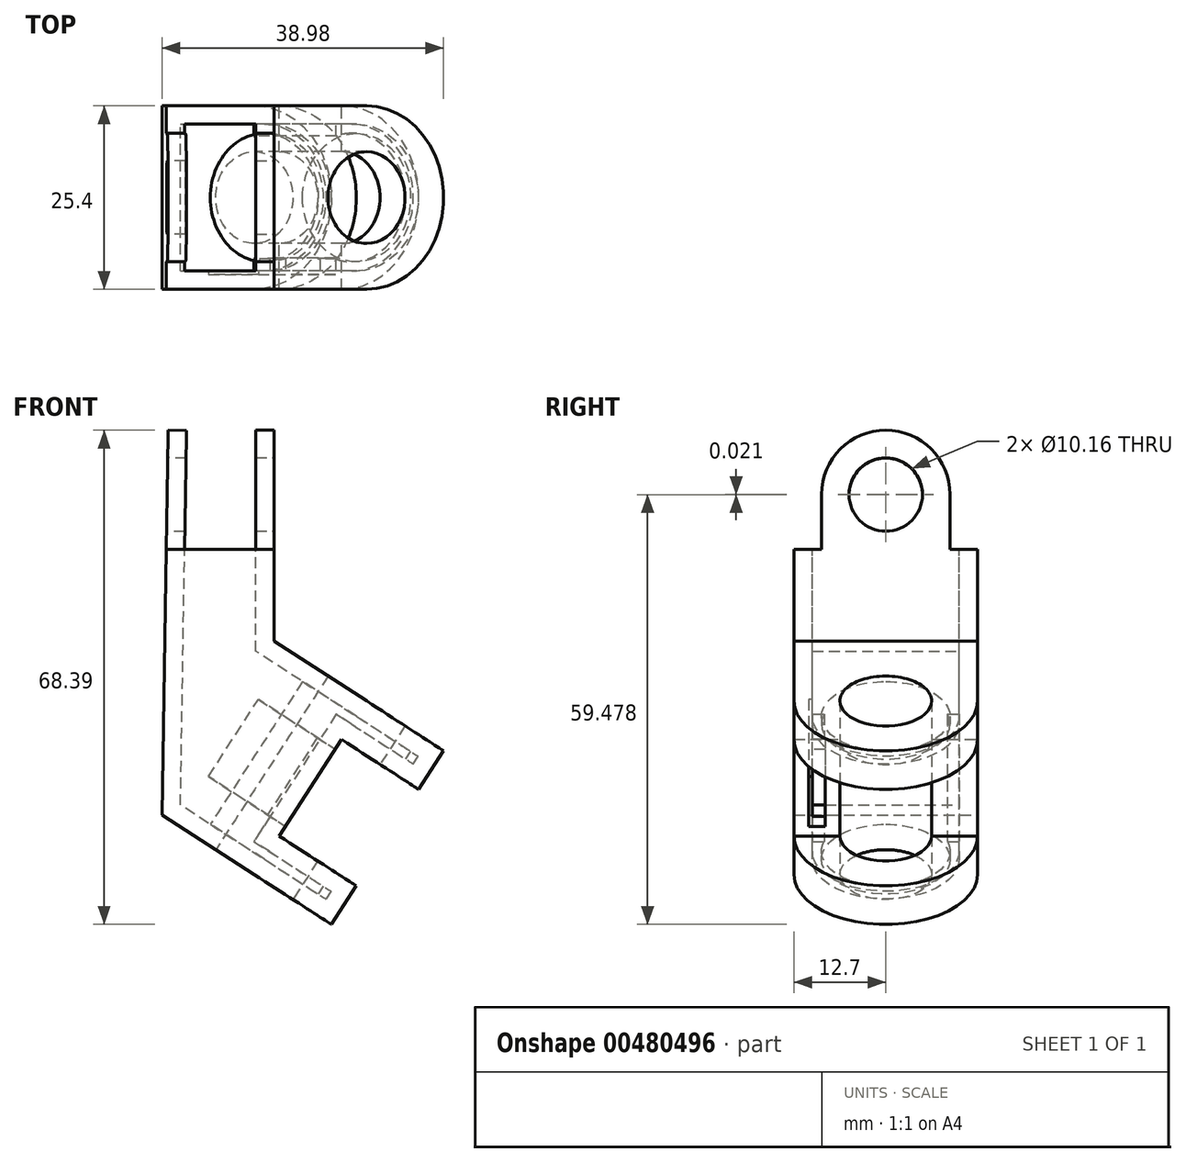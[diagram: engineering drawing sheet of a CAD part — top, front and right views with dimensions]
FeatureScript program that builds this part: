
annotation { "Feature Type Name" : "Feature", "Feature Type Description" : "" }
export const myFeature = defineFeature(function(context is Context, id is Id, definition is map)
    precondition{}
    {
        {
            var Q0;
            Q0=qCreatedBy(makeId("Front.planeOp"),FACE);
            var sketch = newSketch(context, id + "F0", { "sketchPlane" : qUnion([Q0])});
            skLineSegment(sketch, "E0", {"start": v(3.05, 0.95) * mm, "end": v(-9.73, 9.2) * mm});
            skLineSegment(sketch, "E1", {"start": v(-12.48, -23.08) * mm, "end": v(-25.26, -14.82) * mm});
            skLineSegment(sketch, "E2", {"start": v(-9.73, 9.2) * mm, "end": v(-9.73, 21.9) * mm});
            skLineSegment(sketch, "E3", {"start": v(-24.67, 21.9) * mm, "end": v(-9.73, 21.9) * mm});
            skLineSegment(sketch, "E4", {"start": v(-10.92, -20.66) * mm, "end": v(1.49, -1.46) * mm});
            skPoint(sketch, "E5.start.orphan", {"position": v(4.25, -16.85) * mm});
            skLineSegment(sketch, "E6", {"start": v(-10.92, -20.66) * mm, "end": v(-12.48, -23.08) * mm});
            skLineSegment(sketch, "E7", {"start": v(-12.48, -23.08) * mm, "end": v(3.05, 0.95) * mm});
            skPoint(sketch, "E8.orphan", {"position": v(-3.52, -28.87) * mm});
            skPoint(sketch, "E9.start.orphan", {"position": v(-1.96, -26.45) * mm});
            skPoint(sketch, "E10.start.orphan", {"position": v(10.45, -7.25) * mm});
            skPoint(sketch, "E11.orphan", {"position": v(12, -4.84) * mm});
            skLineSegment(sketch, "E12", {"start": v(-25.26, -14.82) * mm, "end": v(-24.67, 21.9) * mm});
            skSolve(sketch);
        }
        {
            var Q0;
            Q0 = qSketchRegion(id + "F0", true);
            extrude(context, id + "F1", {"entities" : qUnion([Q0]), "depth" : 25.4 * mm});
        }
        {
            var Q0;
            Q0=makeQuery(id+"F1.opExtrude","SWEPT_FACE",FACE,{"disambiguationData":[OSD([sQuery(id+"F0.wireOp",EDGE,"E0")])]});
            var sketch = newSketch(context, id + "F2", { "sketchPlane" : qUnion([Q0])});
            skLineSegment(sketch, "E13", {"start": v(2.04, -25.4) * mm, "end": v(2.04, -17.78) * mm});
            skArc(sketch, "E14", {"start": v(2.04, -25.4) * mm, "mid": v(14.74, -12.7) * mm, "end": v(2.04, 0) * mm});
            skCircle(sketch, "E15", {"center": v(2.04, -12.7) * mm, "radius": 5.08 * mm});
            skLineSegment(sketch, "E16.trimOffspring", {"start": v(2.04, -7.62) * mm, "end": v(2.04, 0) * mm});
            skSolve(sketch);
        }
        {
            var Q0;
            {var subQ0=sQuery(id+"F2.wireOp",EDGE,"E13");Q0=makeQuery(id+"F2.imprint","IMPRINT",FACE,{"disambiguationData":[TD([[makeQuery(id+"F2.imprint","IMPRINT",EDGE,{"derivedFrom":subQ0}),-1.0]])]});}
            extrude(context, id + "F3", {"entities" : qUnion([Q0]), "operationType" : NewBodyOperationType.ADD, "depth" : -6.35 * mm});
        }
        {
            var Q0;
            Q0=makeQuery(id+"F1.opExtrude","SWEPT_FACE",FACE,{"disambiguationData":[OSD([sQuery(id+"F0.wireOp",EDGE,"E1")])]});
            var sketch = newSketch(context, id + "F4", { "sketchPlane" : qUnion([Q0])});
            skArc(sketch, "E17", {"start": v(2.04, 0) * mm, "mid": v(14.74, 12.7) * mm, "end": v(2.04, 25.4) * mm});
            skCircle(sketch, "E18", {"center": v(2.04, 12.7) * mm, "radius": 6.35 * mm});
            skSolve(sketch);
        }
        {
            var Q0;
            {var subQ0=sQuery(id+"F4.wireOp",EDGE,"E17");Q0=makeQuery(id+"F4.imprint","IMPRINT",FACE,{"disambiguationData":[TD([[makeQuery(id+"F4.imprint","IMPRINT",EDGE,{"derivedFrom":subQ0}),1.0]])]});}
            extrude(context, id + "F5", {"entities" : qUnion([Q0]), "operationType" : NewBodyOperationType.ADD, "depth" : -6.35 * mm});
        }
        {
            var Q0;
            Q0=sQuery(id+"F4.wireOp",VERTEX,"E17.center");
            var Q1;
            Q1=makeQuery(id+"F1.opExtrude","SWEPT_BODY",BODY,{"disambiguationData":[OSD([sQuery(id+"F0.wireOp",EDGE,"E0"),sQuery(id+"F0.wireOp",EDGE,"E1"),sQuery(id+"F0.wireOp",EDGE,"E2"),sQuery(id+"F0.wireOp",EDGE,"91f72571-9d86-468c-b467-24505ed81b32"),sQuery(id+"F0.wireOp",EDGE,"E3"),sQuery(id+"F0.wireOp",EDGE,"E7")])]});
            hole(context, id + "F6", {"style" : HoleStyle.SIMPLE, "endStyle" : HoleEndStyle.THROUGH, "holeDiameter" : 12.7 * mm, "isTappedThrough" : true, "tappedDepth" : 12.7 * mm, "tapClearance" : 3, "locations" : qUnion([Q0]), "scope" : qUnion([Q1])});
        }
        {
            var Q0;
            Q0=makeQuery(id+"F1.opExtrude","SWEPT_FACE",FACE,{"disambiguationData":[OSD([sQuery(id+"F0.wireOp",EDGE,"E3")])]});
            shell(context, id + "F7", {"entities" : qUnion([Q0]), "thickness" : 2.54 * mm});
        }
        {
            var Q0;
            Q0=makeQuery(id+"F1.opExtrude","SWEPT_FACE",FACE,{"disambiguationData":[OSD([sQuery(id+"F0.wireOp",EDGE,"E2")])]});
            var sketch = newSketch(context, id + "F8", { "sketchPlane" : qUnion([Q0])});
            skLineSegment(sketch, "E19", {"start": v(-12.7, 21.9) * mm, "end": v(-12.7, 29.53) * mm});
            skLineSegment(sketch, "E20", {"start": v(-21.6, 21.9) * mm, "end": v(-21.6, 29.53) * mm});
            skLineSegment(sketch, "E21", {"start": v(-3.81, 21.9) * mm, "end": v(-3.81, 29.53) * mm});
            skArc(sketch, "E22", {"start": v(-3.8, 29.53) * mm, "mid": v(-12.7, 38.42) * mm, "end": v(-21.6, 29.53) * mm});
            skCircle(sketch, "E23", {"center": v(-12.7, 29.53) * mm, "radius": 5.08 * mm});
            skSolve(sketch);
        }
        {
            var Q0;
            {var subQ1=sQuery(id+"F8.wireOp",EDGE,"E20");Q0=makeQuery(id+"F8.imprint","IMPRINT",FACE,{"disambiguationData":[TD([[makeQuery(id+"F8.imprint","IMPRINT",EDGE,{"derivedFrom":subQ1}),-1.0]])]});}
            extrude(context, id + "F9", {"entities" : qUnion([Q0]), "operationType" : NewBodyOperationType.ADD, "depth" : -2.54 * mm});
        }
        {
            var Q0;
            Q0=makeQuery(id+"F1.opExtrude","SWEPT_FACE",FACE,{"disambiguationData":[OSD([sQuery(id+"F0.wireOp",EDGE,"E12")])]});
            var sketch = newSketch(context, id + "F10", { "sketchPlane" : qUnion([Q0])});
            skLineSegment(sketch, "E24", {"start": v(3.81, 21.51) * mm, "end": v(3.81, 29.13) * mm});
            skLineSegment(sketch, "E25", {"start": v(21.6, 21.51) * mm, "end": v(21.6, 29.13) * mm});
            skArc(sketch, "E26", {"start": v(21.6, 29.13) * mm, "mid": v(12.7, 38.02) * mm, "end": v(3.81, 29.13) * mm});
            skCircle(sketch, "E27", {"center": v(12.7, 29.13) * mm, "radius": 5.08 * mm});
            skLineSegment(sketch, "E28", {"start": v(3.81, 29.13) * mm, "end": v(7.62, 29.13) * mm});
            skPoint(sketch, "E29.start.orphan", {"position": v(12.7, 21.51) * mm});
            skLineSegment(sketch, "E30.trimOffspring", {"start": v(12.7, 29.13) * mm, "end": v(21.6, 29.13) * mm});
            skSolve(sketch);
        }
        {
            var Q0;
            {var subQ5=sQuery(id+"F10.wireOp",EDGE,"E24");Q0=makeQuery(id+"F10.imprint","IMPRINT",FACE,{"disambiguationData":[TD([[makeQuery(id+"F10.imprint","IMPRINT",EDGE,{"derivedFrom":subQ5}),-1.0]])]});}
            var Q1;
            {var subQ0=sQuery(id+"F10.wireOp",EDGE,"E26");Q1=makeQuery(id+"F10.imprint","IMPRINT",FACE,{"disambiguationData":[TD([[makeQuery(id+"F10.imprint","IMPRINT",EDGE,{"derivedFrom":subQ0}),1.0]])]});}
            extrude(context, id + "F11", {"entities" : qUnion([Q0, Q1]), "operationType" : NewBodyOperationType.ADD, "depth" : -2.54 * mm});
        }
        {
            var Q0;
            {var subQ2=sQuery(id+"F0.wireOp",EDGE,"E7");var subQ3=sQuery(id+"F0.wireOp",EDGE,"E1");Q0=makeQuery(id+"F6.hole-0.boolean.opBoolean","SPLIT",FACE,{"disambiguationData":[TD([makeQuery(id+"F1.opExtrude","CAP_FACE",FACE,{"disambiguationData":[OSD([sQuery(id+"F0.wireOp",EDGE,"E0"),subQ3,sQuery(id+"F0.wireOp",EDGE,"E2"),sQuery(id+"F0.wireOp",EDGE,"E3"),subQ2,sQuery(id+"F0.wireOp",EDGE,"E12")])],"isStart":false})])],"derivedFrom":makeQuery(id+"F1.opExtrude","SWEPT_FACE",FACE,{"disambiguationData":[OSD([subQ2])]})});}
            var sketch = newSketch(context, id + "F12", { "sketchPlane" : qUnion([Q0])});
            skLineSegment(sketch, "E31", {"start": v(-25.4, -11.85) * mm, "end": v(-19.05, -11.85) * mm});
            skLineSegment(sketch, "E32.bottom", {"start": v(-21.08, -5.5) * mm, "end": v(-23.37, -5.5) * mm});
            skLineSegment(sketch, "E32.top", {"start": v(-21.08, -18.2) * mm, "end": v(-23.37, -18.2) * mm});
            skLineSegment(sketch, "E32.left", {"start": v(-21.08, -5.5) * mm, "end": v(-21.08, -18.2) * mm});
            skLineSegment(sketch, "E32.right", {"start": v(-23.37, -5.5) * mm, "end": v(-23.37, -18.2) * mm});
            skPoint(sketch, "E32.middle", {"position": v(-22.23, -11.85) * mm});
            skSolve(sketch);
        }
        {
            var Q0;
            {var subQ5=sQuery(id+"F12.wireOp",EDGE,"E32.top");Q0=makeQuery(id+"F12.imprint","IMPRINT",FACE,{"disambiguationData":[TD([[makeQuery(id+"F12.imprint","IMPRINT",EDGE,{"derivedFrom":subQ5}),-1.0]])]});}
            var Q1;
            {var subQ5=sQuery(id+"F12.wireOp",EDGE,"E32.bottom");Q1=makeQuery(id+"F12.imprint","IMPRINT",FACE,{"disambiguationData":[TD([[makeQuery(id+"F12.imprint","IMPRINT",EDGE,{"derivedFrom":subQ5}),1.0]])]});}
            extrude(context, id + "F13", {"entities" : qUnion([Q0, Q1]), "operationType" : NewBodyOperationType.REMOVE, "oppositeDirection" : true, "depth" : 12.7 * mm});
        }
    });
